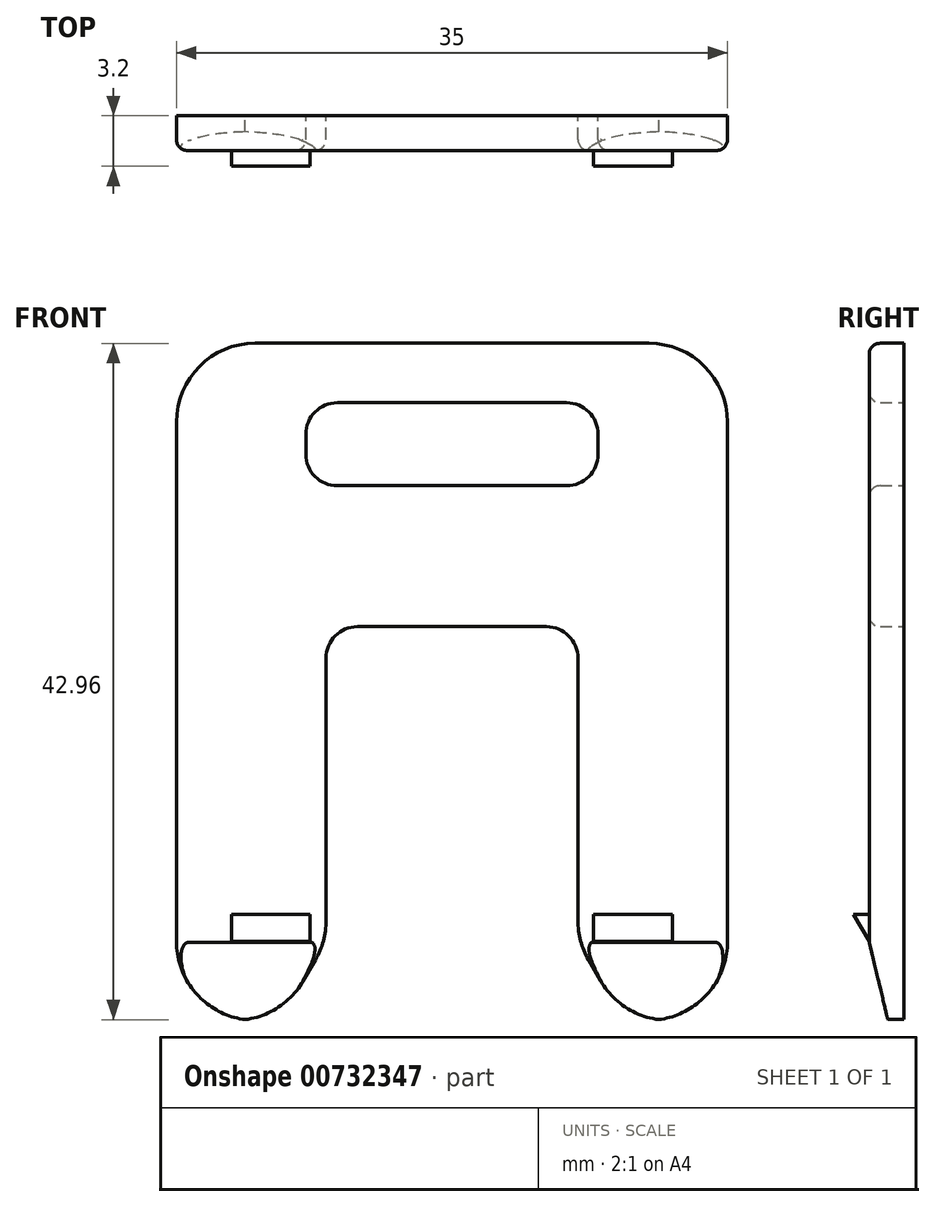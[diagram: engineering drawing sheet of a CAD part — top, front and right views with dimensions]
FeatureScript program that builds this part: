
annotation { "Feature Type Name" : "Feature", "Feature Type Description" : "" }
export const myFeature = defineFeature(function(context is Context, id is Id, definition is map)
    precondition{}
    {
        {
            var Q0;
            Q0=qCreatedBy(makeId("Front.planeOp"),FACE);
            var sketch = newSketch(context, id + "F0", { "sketchPlane" : qUnion([Q0])});
            skLineSegment(sketch, "E0", {"start": v(-71.37, 62.57) * mm, "end": v(-71.37, 29.57) * mm});
            skLineSegment(sketch, "E1", {"start": v(-67.64, 24.57) * mm, "end": v(-66.37, 24.57) * mm});
            skLineSegment(sketch, "E2", {"start": v(-63.31, 27.07) * mm, "end": v(-62.54, 28.41) * mm});
            skLineSegment(sketch, "E3", {"start": v(-61.87, 30.91) * mm, "end": v(-61.87, 47.57) * mm});
            skLineSegment(sketch, "E4", {"start": v(-59.87, 49.57) * mm, "end": v(-47.87, 49.57) * mm});
            skLineSegment(sketch, "E5", {"start": v(-45.87, 47.57) * mm, "end": v(-45.87, 30.91) * mm});
            skLineSegment(sketch, "E6", {"start": v(-44.43, 27.07) * mm, "end": v(-45.2, 28.41) * mm});
            skLineSegment(sketch, "E7", {"start": v(-41.37, 24.57) * mm, "end": v(-40.1, 24.57) * mm});
            skLineSegment(sketch, "E8", {"start": v(-36.37, 29.57) * mm, "end": v(-36.37, 62.57) * mm});
            skLineSegment(sketch, "E9", {"start": v(-41.37, 67.57) * mm, "end": v(-66.37, 67.57) * mm});
            skLineSegment(sketch, "E10", {"start": v(-53.87, 79.57) * mm, "end": v(-53.87, -17.6) * mm, "construction": true});
            skPoint(sketch, "E10.startSnap0", {"position": v(-53.87, 67.57) * mm});
            skPoint(sketch, "E11.visualSharp", {"position": v(-61.87, 29.57) * mm});
            skArc(sketch, "E11.filletArc", {"start": v(-62.54, 28.41) * mm, "mid": v(-62.04, 29.62) * mm, "end": v(-61.87, 30.91) * mm});
            skPoint(sketch, "E12.visualSharp", {"position": v(-45.87, 29.57) * mm});
            skArc(sketch, "E12.filletArc", {"start": v(-45.87, 30.91) * mm, "mid": v(-45.7, 29.62) * mm, "end": v(-45.2, 28.41) * mm});
            skPoint(sketch, "E13.visualSharp", {"position": v(-42.98, 24.57) * mm});
            skArc(sketch, "E13.filletArc", {"start": v(-44.43, 27.07) * mm, "mid": v(-42.6, 25.24) * mm, "end": v(-40.1, 24.57) * mm});
            skPoint(sketch, "E14.visualSharp", {"position": v(-64.76, 24.57) * mm});
            skArc(sketch, "E14.filletArc", {"start": v(-67.64, 24.57) * mm, "mid": v(-65.14, 25.24) * mm, "end": v(-63.31, 27.07) * mm});
            skPoint(sketch, "E15.visualSharp", {"position": v(-36.37, 24.57) * mm});
            skArc(sketch, "E15.filletArc", {"start": v(-41.37, 24.57) * mm, "mid": v(-37.83, 26.04) * mm, "end": v(-36.37, 29.57) * mm});
            skPoint(sketch, "E16.visualSharp", {"position": v(-36.37, 67.57) * mm});
            skArc(sketch, "E16.filletArc", {"start": v(-36.37, 62.57) * mm, "mid": v(-37.83, 66.1) * mm, "end": v(-41.37, 67.57) * mm});
            skPoint(sketch, "E17.visualSharp", {"position": v(-71.37, 67.57) * mm});
            skArc(sketch, "E17.filletArc", {"start": v(-66.37, 67.57) * mm, "mid": v(-69.9, 66.1) * mm, "end": v(-71.37, 62.57) * mm});
            skPoint(sketch, "E18.visualSharp", {"position": v(-71.37, 24.57) * mm});
            skArc(sketch, "E18.filletArc", {"start": v(-71.37, 29.57) * mm, "mid": v(-69.9, 26.04) * mm, "end": v(-66.37, 24.57) * mm});
            skLineSegment(sketch, "E19.bottom", {"start": v(-61.15, 63.8) * mm, "end": v(-46.59, 63.8) * mm});
            skLineSegment(sketch, "E19.top", {"start": v(-61.15, 58.52) * mm, "end": v(-46.59, 58.52) * mm});
            skLineSegment(sketch, "E19.left", {"start": v(-63.15, 61.8) * mm, "end": v(-63.15, 60.52) * mm});
            skLineSegment(sketch, "E19.right", {"start": v(-44.59, 61.8) * mm, "end": v(-44.59, 60.52) * mm});
            skPoint(sketch, "E20.visualSharp", {"position": v(-63.15, 63.8) * mm});
            skArc(sketch, "E20.filletArc", {"start": v(-61.15, 63.8) * mm, "mid": v(-62.56, 63.21) * mm, "end": v(-63.15, 61.8) * mm});
            skPoint(sketch, "E21.visualSharp", {"position": v(-63.15, 58.52) * mm});
            skArc(sketch, "E21.filletArc", {"start": v(-63.15, 60.52) * mm, "mid": v(-62.56, 59.1) * mm, "end": v(-61.15, 58.52) * mm});
            skPoint(sketch, "E22.visualSharp", {"position": v(-44.59, 58.52) * mm});
            skArc(sketch, "E22.filletArc", {"start": v(-46.59, 58.52) * mm, "mid": v(-45.17, 59.1) * mm, "end": v(-44.59, 60.52) * mm});
            skPoint(sketch, "E23.visualSharp", {"position": v(-44.59, 63.8) * mm});
            skArc(sketch, "E23.filletArc", {"start": v(-44.59, 61.8) * mm, "mid": v(-45.17, 63.21) * mm, "end": v(-46.59, 63.8) * mm});
            skPoint(sketch, "E24.visualSharp", {"position": v(-61.87, 49.57) * mm});
            skArc(sketch, "E24.filletArc", {"start": v(-59.87, 49.57) * mm, "mid": v(-61.28, 48.99) * mm, "end": v(-61.87, 47.57) * mm});
            skPoint(sketch, "E25.visualSharp", {"position": v(-45.87, 49.57) * mm});
            skArc(sketch, "E25.filletArc", {"start": v(-45.87, 47.57) * mm, "mid": v(-46.45, 48.99) * mm, "end": v(-47.87, 49.57) * mm});
            skSolve(sketch);
        }
        {
            var Q0;
            Q0=makeQuery(id+"F0.imprint","IMPRINT",FACE,{"disambiguationData":[TD([[makeQuery(id+"F0.imprint","IMPRINT",EDGE,{"derivedFrom":sQuery(id+"F0.wireOp",EDGE,"E0")}),1.0]])]});
            extrude(context, id + "F1", {"entities" : qUnion([Q0]), "depth" : 2.2 * mm, "offsetDistance" : 25 * mm});
        }
        {
            var Q0;
            Q0=makeQuery(id+"F1.opExtrude","SWEPT_FACE",FACE,{"disambiguationData":[OSD([sQuery(id+"F0.wireOp",EDGE,"E0")])]});
            var sketch = newSketch(context, id + "F2", { "sketchPlane" : qUnion([Q0])});
            skLineSegment(sketch, "E26", {"start": v(2.2, 29.52) * mm, "end": v(0, 20.41) * mm});
            skLineSegment(sketch, "E27", {"start": v(0, 20.41) * mm, "end": v(7.19, 20.41) * mm});
            skLineSegment(sketch, "E28", {"start": v(7.19, 20.41) * mm, "end": v(7.19, 29.52) * mm});
            skLineSegment(sketch, "E29", {"start": v(7.19, 29.52) * mm, "end": v(2.2, 29.52) * mm});
            skSolve(sketch);
        }
        {
            var Q0;
            {var subQ0=sQuery(id+"F2.wireOp",EDGE,"E26");var subQ1=sQuery(id+"F0.wireOp",EDGE,"E0");var subQ2=makeQuery(id+"F1.opExtrude","CAP_EDGE",EDGE,{"disambiguationData":[OSD([subQ1])],"isStart":false});var subQ3=makeQuery(id+"F2.imprint","INTERSECT",VERTEX,{"derivedFrom":[subQ2,subQ0,sQuery(id+"F2.wireOp",EDGE,"E29")]});Q0=makeQuery(id+"F2.imprint","IMPRINT",FACE,{"disambiguationData":[TD([[makeQuery(id+"F2.imprint","IMPRINT",EDGE,{"disambiguationData":[TD([[subQ3,-1.0]])],"derivedFrom":subQ0}),1.0]])]});}
            var Q1;
            {var subQ1=sQuery(id+"F2.wireOp",EDGE,"E27");Q1=makeQuery(id+"F2.imprint","IMPRINT",FACE,{"disambiguationData":[TD([[makeQuery(id+"F2.imprint","IMPRINT",EDGE,{"derivedFrom":subQ1}),1.0]])]});}
            extrude(context, id + "F3", {"entities" : qUnion([Q0, Q1]), "operationType" : NewBodyOperationType.REMOVE, "endBound" : BoundingType.THROUGH_ALL, "oppositeDirection" : true, "depth" : 25 * mm, "offsetDistance" : 25 * mm});
        }
        {
            var Q0;
            Q0=makeQuery(id+"F1.opExtrude","SWEPT_FACE",FACE,{"disambiguationData":[OSD([sQuery(id+"F0.wireOp",EDGE,"E0")])]});
            var sketch = newSketch(context, id + "F4", { "sketchPlane" : qUnion([Q0])});
            skLineSegment(sketch, "E30.0", {"start": v(0, 47.57) * mm, "end": v(0, 30.91) * mm});
            skLineSegment(sketch, "E31", {"start": v(2.2, 29.57) * mm, "end": v(3.2, 31.3) * mm});
            skLineSegment(sketch, "E32", {"start": v(3.2, 31.3) * mm, "end": v(2.2, 31.3) * mm});
            skSolve(sketch);
        }
        {
            var Q0;
            Q0 = qSketchRegion(id + "F4", true);
            var Q1;
            {var subQ0=sQuery(id+"F4.wireOp",EDGE,"E31");Q1=makeQuery(id+"F4.imprint","IMPRINT",FACE,{"disambiguationData":[TD([[makeQuery(id+"F4.imprint","IMPRINT",EDGE,{"derivedFrom":subQ0}),1.0]])]});}
            extrude(context, id + "F5", {"entities" : qUnion([Q0, Q1]), "operationType" : NewBodyOperationType.ADD, "oppositeDirection" : true, "depth" : 8.5 * mm, "offsetDistance" : 25 * mm, "hasSecondDirection" : true, "secondDirectionOppositeDirection" : true, "secondDirectionDepth" : 3.5 * mm});
        }
        {
            var Q0;
            {var subQ0=sQuery(id+"F4.wireOp",EDGE,"E31");Q0=makeQuery(id+"F4.imprint","IMPRINT",FACE,{"disambiguationData":[TD([[makeQuery(id+"F4.imprint","IMPRINT",EDGE,{"derivedFrom":subQ0}),1.0]])]});}
            extrude(context, id + "F6", {"entities" : qUnion([Q0]), "operationType" : NewBodyOperationType.ADD, "oppositeDirection" : true, "depth" : 31.5 * mm, "offsetDistance" : 25 * mm, "hasSecondDirection" : true, "secondDirectionOppositeDirection" : true, "secondDirectionDepth" : 26.5 * mm});
        }
        {
            var Q0;
            Q0=makeQuery(id+"F1.opExtrude","CAP_EDGE",EDGE,{"disambiguationData":[OSD([sQuery(id+"F0.wireOp",EDGE,"E3")])],"isStart":false});
            var Q1;
            Q1=makeQuery(id+"F1.opExtrude","CAP_EDGE",EDGE,{"disambiguationData":[OSD([sQuery(id+"F0.wireOp",EDGE,"E0")])],"isStart":false});
            var Q2;
            Q2=makeQuery(id+"F1.opExtrude","CAP_EDGE",EDGE,{"disambiguationData":[OSD([sQuery(id+"F0.wireOp",EDGE,"E19.top")])],"isStart":false});
            fillet(context, id + "F7", {"entities" : qUnion([Q0, Q1, Q2]), "radius" : 0.7 * mm, "tangentPropagation" : true, "allowEdgeOverflow" : false});
        }
    });
